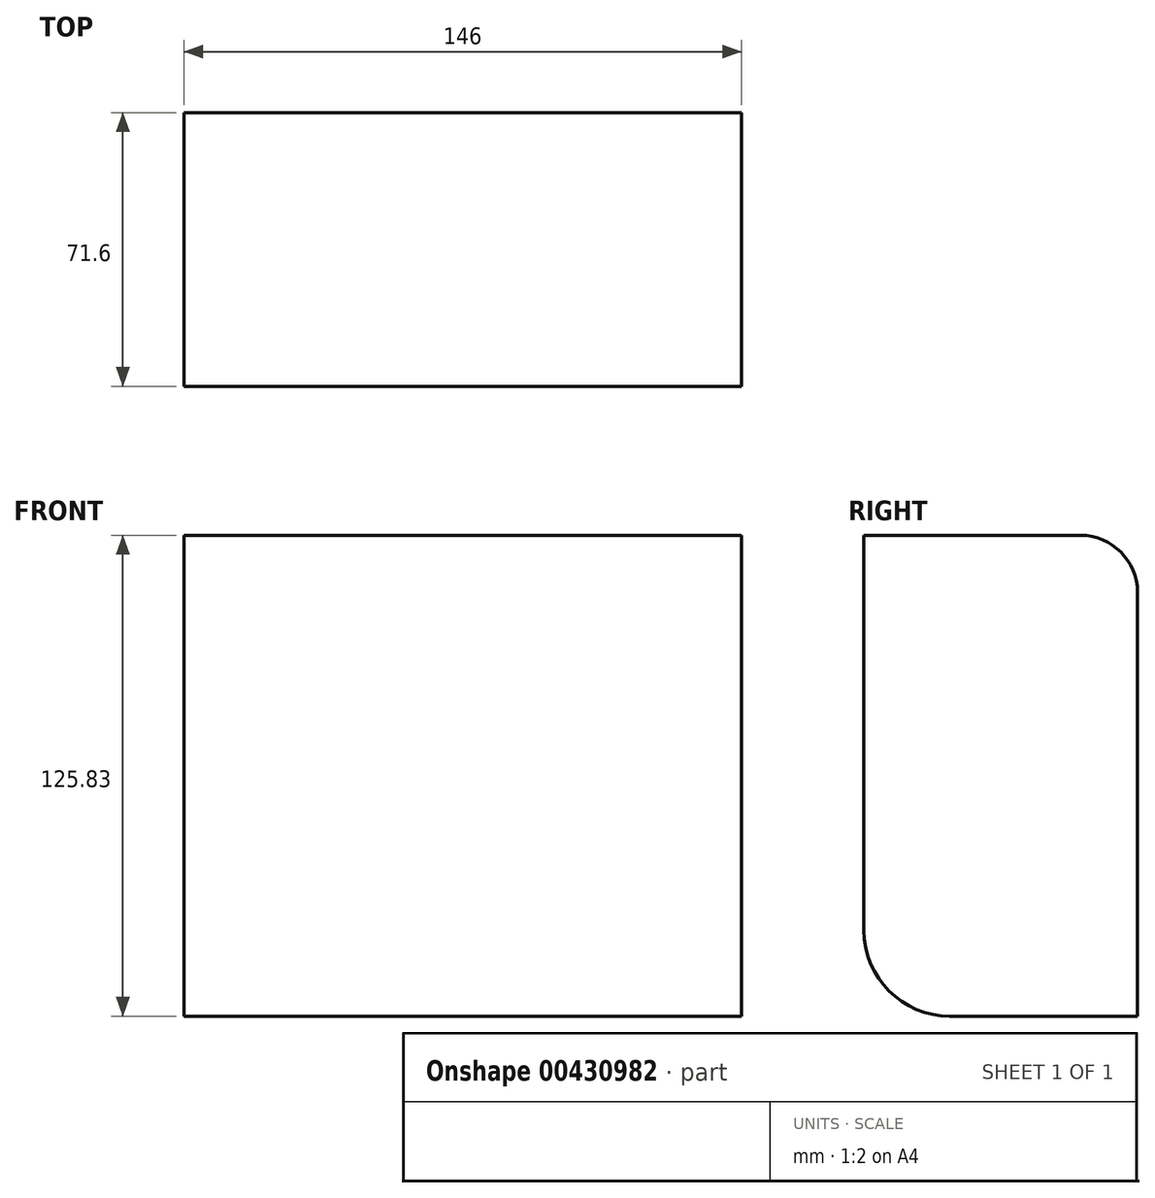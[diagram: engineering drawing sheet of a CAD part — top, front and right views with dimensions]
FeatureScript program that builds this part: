
annotation { "Feature Type Name" : "Feature", "Feature Type Description" : "" }
export const myFeature = defineFeature(function(context is Context, id is Id, definition is map)
    precondition{}
    {
        {
            var Q0;
            Q0=qCreatedBy(makeId("Right.planeOp"),FACE);
            var sketch = newSketch(context, id + "F0", { "sketchPlane" : qUnion([Q0])});
            skLineSegment(sketch, "E0.bottom", {"start": v(-18.33, 72.4) * mm, "end": v(38.37, 72.4) * mm});
            skLineSegment(sketch, "E0.top", {"start": v(4.12, -53.42) * mm, "end": v(53.27, -53.42) * mm});
            skLineSegment(sketch, "E0.left", {"start": v(-18.33, 72.4) * mm, "end": v(-18.33, -30.96) * mm});
            skLineSegment(sketch, "E0.right", {"start": v(53.27, 57.5) * mm, "end": v(53.27, -53.42) * mm});
            skPoint(sketch, "E1.visualSharp", {"position": v(53.27, 72.4) * mm});
            skArc(sketch, "E1.filletArc", {"start": v(53.27, 57.5) * mm, "mid": v(48.9, 68.04) * mm, "end": v(38.37, 72.4) * mm});
            skPoint(sketch, "E2.visualSharp", {"position": v(-18.33, -53.42) * mm});
            skArc(sketch, "E2.filletArc", {"start": v(-18.33, -30.96) * mm, "mid": v(-11.75, -46.84) * mm, "end": v(4.12, -53.42) * mm});
            skSolve(sketch);
        }
        {
            var Q0;
            Q0 = qSketchRegion(id + "F0", true);
            extrude(context, id + "F1", {"entities" : qUnion([Q0]), "depth" : 146 * mm});
        }
    });
